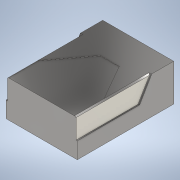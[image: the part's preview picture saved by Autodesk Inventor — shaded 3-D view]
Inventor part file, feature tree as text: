
AUTODESK INVENTOR PART (.ipt)
format: ipt  version: 2020 (Build 240168000, 168)  size: 167,424 bytes
history: native  units: in
note: dims shown in document units (in); Inventor stores cm internally (conversion verified against a paired STEP export)
features: extrude x5, sketch x5, chamfer x2
ambient origin geometry x8: Origin, YZ Plane, XZ Plane, XY Plane, X Axis, Y Axis, Z Axis, Center Point
bodies: Solid1 (feature_tree)
feature tree (12):
  extrude  "Extrusion1"  Depth=1.1304in
  extrude  "Extrusion2"  Depth=0.0984in
  extrude  "Extrusion3"  Depth=0.0591in
  chamfer  "Chamfer1"  Distance=0.1181in
  extrude  "Extrusion4"  Depth=0.0591in
  chamfer  "Chamfer2"  Distance=0.0591in
  extrude  "Extrusion5"  Depth=1.378in TaperAngle=0.0deg
  sketch  "Sketch1"  dims[d0=1.5354in d1=1.1304in]
  sketch  "Sketch2"  dims[d2=0.5906in d3=0.0in d7=0.0984in]
  sketch  "Sketch3"  dims[d8=0.1181in d9=0.0591in]
  sketch  "Sketch4"  dims[d10=0.0591in]
  sketch  "Sketch5"  dims[d11=0.0984in d12=0.1181in d13=0.0591in d14=0.0591in d15=1.378in d16=0.0in d17=0.0197in d18=0.0in d19=0.0079in d20=0.0787in d21=45.0deg d22=0.0197in d23=0.0in d24=0.0197in d25=0.0787in d26=45.0deg d27=0.0079in d28=0.0in]
